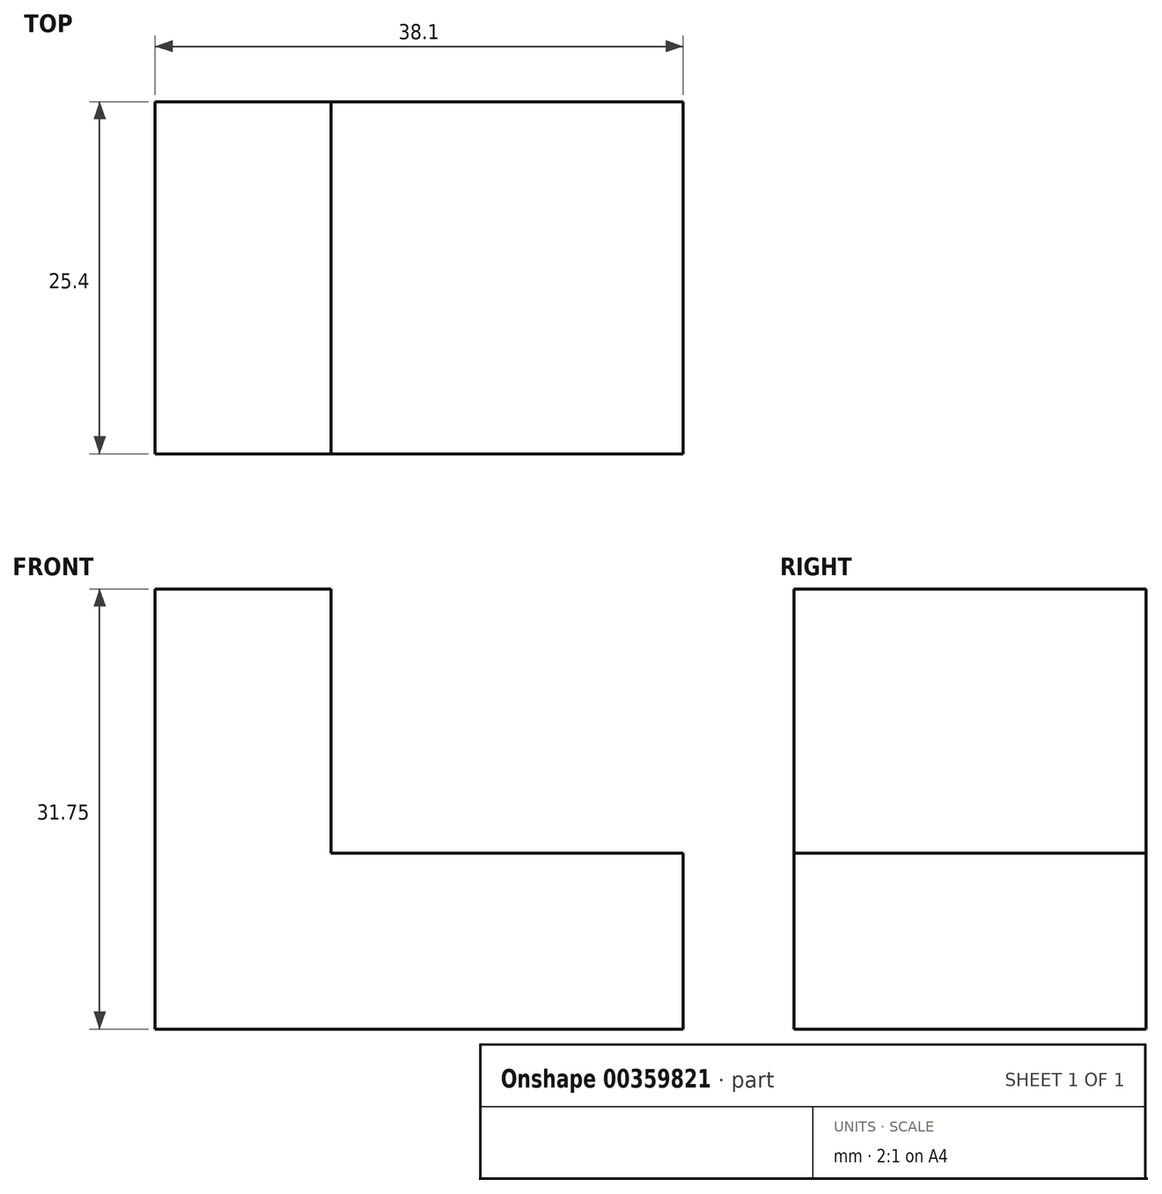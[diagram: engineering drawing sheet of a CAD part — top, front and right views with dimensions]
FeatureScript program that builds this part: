
annotation { "Feature Type Name" : "Feature", "Feature Type Description" : "" }
export const myFeature = defineFeature(function(context is Context, id is Id, definition is map)
    precondition{}
    {
        {
            var Q0;
            Q0=qCreatedBy(makeId("Front.planeOp"),FACE);
            var sketch = newSketch(context, id + "F0", { "sketchPlane" : qUnion([Q0])});
            skLineSegment(sketch, "E0", {"start": v(0, 0) * mm, "end": v(0, 31.75) * mm});
            skLineSegment(sketch, "E1", {"start": v(0, 31.75) * mm, "end": v(12.7, 31.75) * mm});
            skLineSegment(sketch, "E2", {"start": v(12.7, 31.75) * mm, "end": v(12.7, 12.7) * mm});
            skLineSegment(sketch, "E3", {"start": v(12.7, 12.7) * mm, "end": v(38.1, 12.7) * mm});
            skLineSegment(sketch, "E4", {"start": v(38.1, 12.7) * mm, "end": v(38.1, 0) * mm});
            skLineSegment(sketch, "E5", {"start": v(38.1, 0) * mm, "end": v(0, 0) * mm});
            skSolve(sketch);
        }
        {
            var Q0;
            Q0=makeQuery(id+"F0.imprint","IMPRINT",FACE,{"disambiguationData":[TD([[makeQuery(id+"F0.imprint","IMPRINT",EDGE,{"derivedFrom":sQuery(id+"F0.wireOp",EDGE,"E0")}),-1.0]])]});
            extrude(context, id + "F1", {"entities" : qUnion([Q0]), "depth" : 25.4 * mm});
        }
    });
